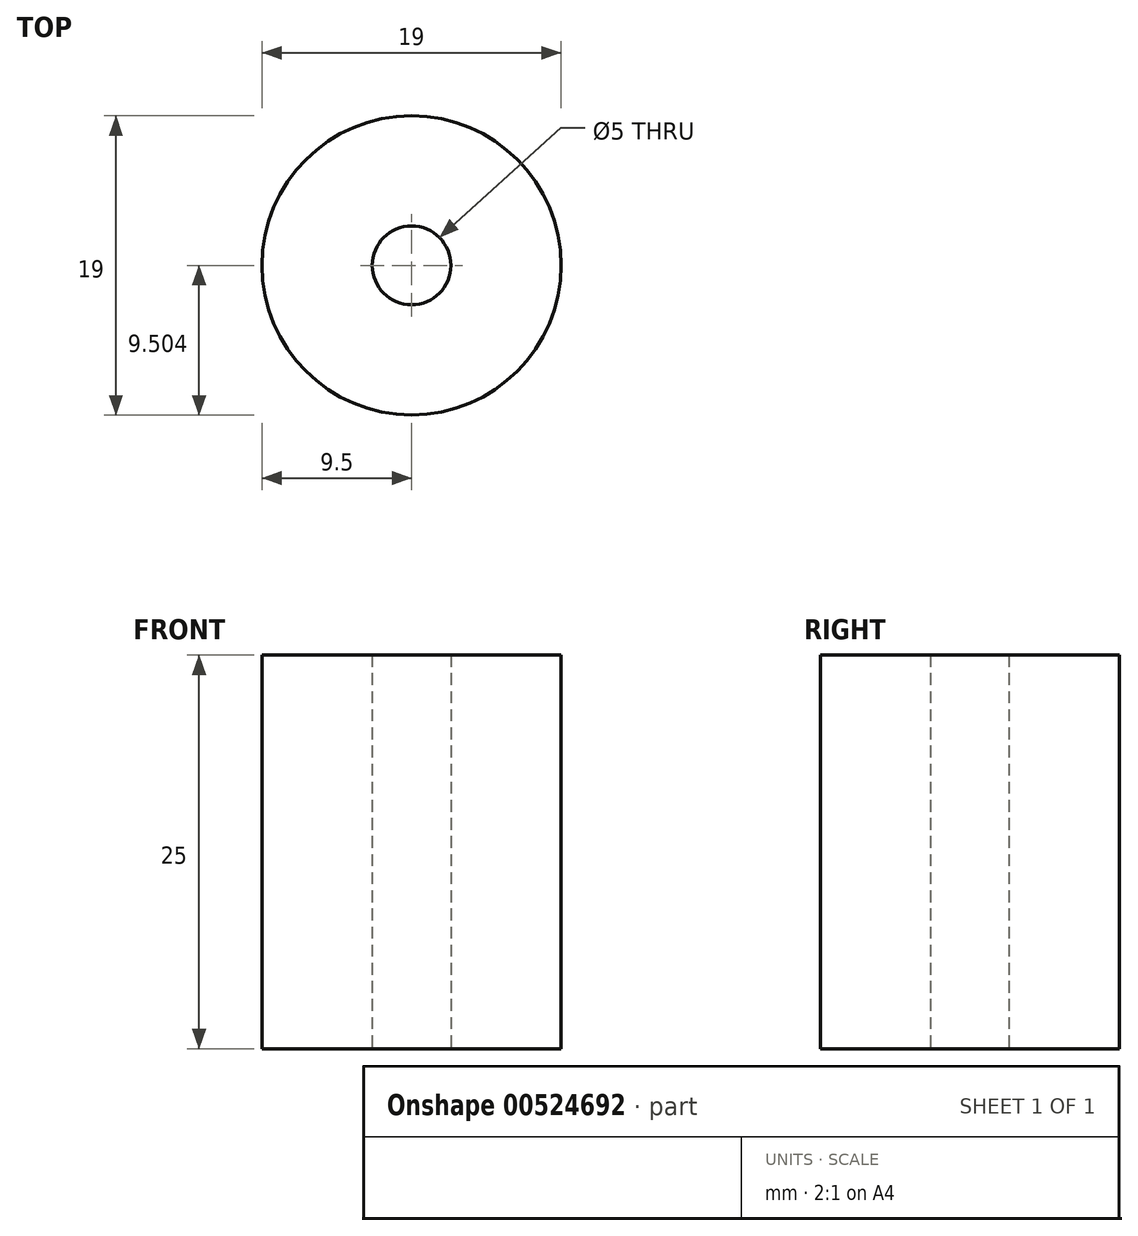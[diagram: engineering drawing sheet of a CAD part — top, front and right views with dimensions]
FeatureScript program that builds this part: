
annotation { "Feature Type Name" : "Feature", "Feature Type Description" : "" }
export const myFeature = defineFeature(function(context is Context, id is Id, definition is map)
    precondition{}
    {
        {
            var Q0;
            Q0=qCreatedBy(makeId("Top.planeOp"),FACE);
            var sketch = newSketch(context, id + "F0", { "sketchPlane" : qUnion([Q0])});
            skCircle(sketch, "E0", {"center": v(-37.44, 10.9) * mm, "radius": 2.5 * mm});
            skCircle(sketch, "E1", {"center": v(-37.44, 10.9) * mm, "radius": 9.5 * mm});
            skSolve(sketch);
        }
        {
            var Q0;
            Q0=makeQuery(id+"F0.imprint","IMPRINT",FACE,{"disambiguationData":[TD([[makeQuery(id+"F0.imprint","IMPRINT",EDGE,{"derivedFrom":sQuery(id+"F0.wireOp",EDGE,"E0")}),-1.0]])]});
            var Q1;
            Q1=makeQuery(id+"F0.imprint","IMPRINT",FACE,{"disambiguationData":[TD([[makeQuery(id+"F0.imprint","IMPRINT",EDGE,{"derivedFrom":sQuery(id+"F0.wireOp",EDGE,"E0")}),1.0]])]});
            extrude(context, id + "F1", {"entities" : qUnion([Q0, Q1]), "depth" : 25 * mm, "offsetDistance" : 25 * mm});
        }
        {
            var Q0;
            Q0=sQuery(id+"F0.wireOp",VERTEX,"E0.center");
            var Q1;
            Q1=makeQuery(id+"F1.opExtrude","SWEPT_BODY",BODY,{"disambiguationData":[OSD([sQuery(id+"F0.wireOp",EDGE,"E1")])]});
            hole(context, id + "F2", {"style" : HoleStyle.SIMPLE, "endStyle" : HoleEndStyle.THROUGH, "oppositeDirection" : true, "holeDiameter" : 5 * mm, "isTappedThrough" : true, "tappedDepth" : 12 * mm, "tapClearance" : 3, "startFromSketch" : true, "locations" : qUnion([Q0]), "scope" : qUnion([Q1])});
        }
    });
